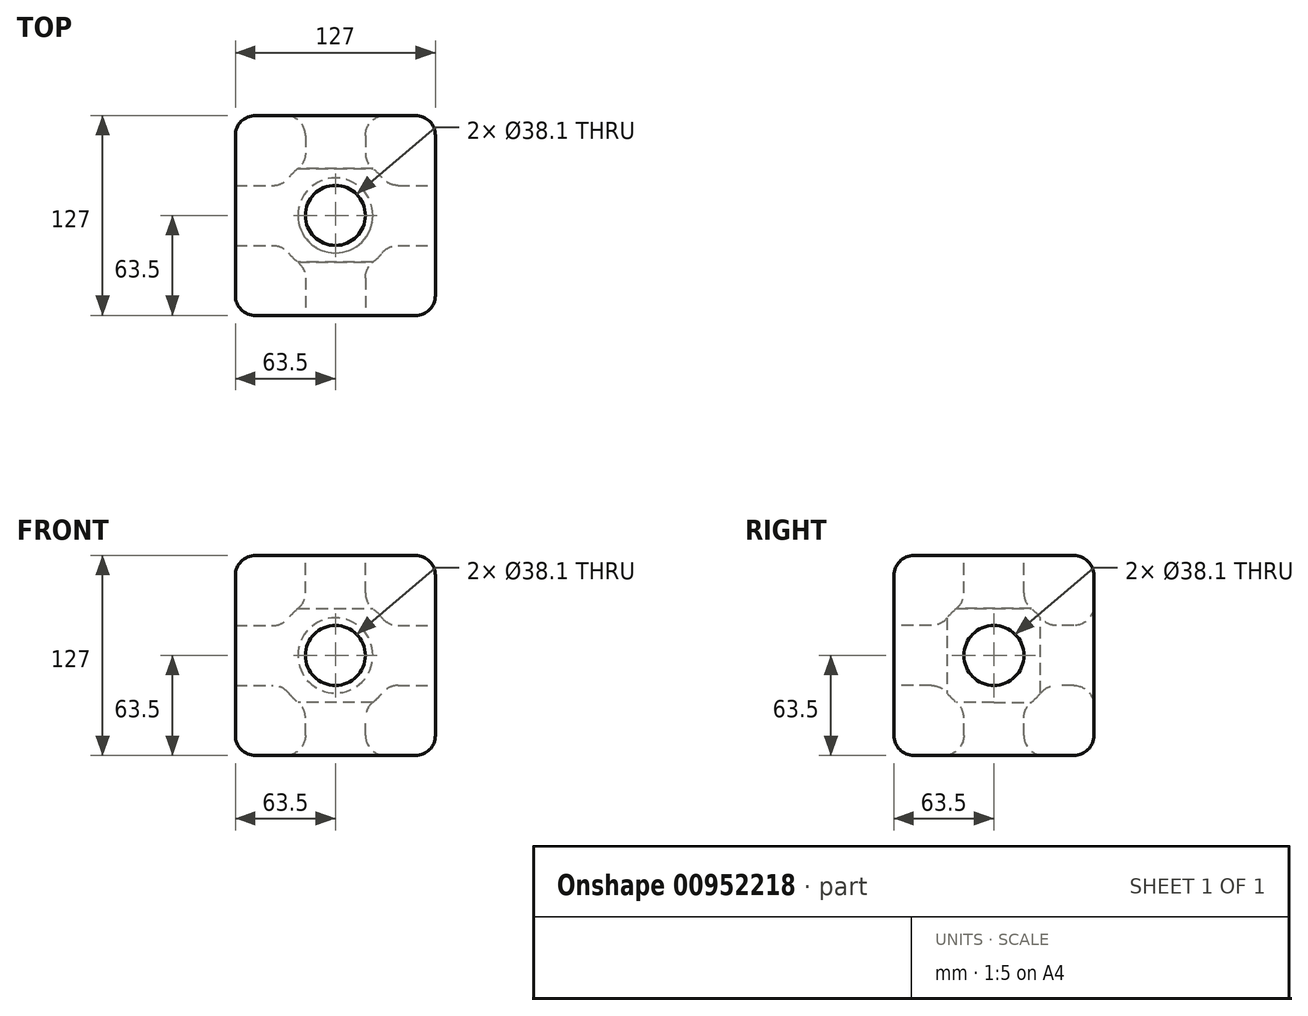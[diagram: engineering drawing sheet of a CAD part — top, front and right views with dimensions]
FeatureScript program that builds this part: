
annotation { "Feature Type Name" : "Feature", "Feature Type Description" : "" }
export const myFeature = defineFeature(function(context is Context, id is Id, definition is map)
    precondition{}
    {
        {
            var Q0;
            Q0=qCreatedBy(makeId("Top.planeOp"),FACE);
            var sketch = newSketch(context, id + "F0", { "sketchPlane" : qUnion([Q0])});
            skLineSegment(sketch, "E0.top", {"start": v(0, 63.5) * mm, "end": v(-63.5, 63.5) * mm});
            skLineSegment(sketch, "E0.right", {"start": v(-63.5, 0) * mm, "end": v(-63.5, 63.5) * mm});
            skLineSegment(sketch, "E1.MirrorCS", {"start": v(0, 63.5) * mm, "end": v(63.5, 63.5) * mm});
            skLineSegment(sketch, "E2.MirrorCS", {"start": v(63.5, 0) * mm, "end": v(63.5, 63.5) * mm});
            skLineSegment(sketch, "E3.MirrorCS", {"start": v(-63.5, 0) * mm, "end": v(-63.5, -63.5) * mm});
            skLineSegment(sketch, "E4.MirrorCS", {"start": v(0, -63.5) * mm, "end": v(-63.5, -63.5) * mm});
            skLineSegment(sketch, "E5.MirrorCS", {"start": v(0, -63.5) * mm, "end": v(63.5, -63.5) * mm});
            skLineSegment(sketch, "E6.MirrorCS", {"start": v(63.5, 0) * mm, "end": v(63.5, -63.5) * mm});
            skSolve(sketch);
        }
        {
            var Q0;
            Q0 = qSketchRegion(id + "F0", true);
            extrude(context, id + "F1", {"entities" : qUnion([Q0]), "endBound" : BoundingType.SYMMETRIC, "depth" : 127 * mm, "offsetDistance" : 25.4 * mm});
        }
        {
            var Q0;
            Q0=qCreatedBy(makeId("Top.planeOp"),FACE);
            var sketch = newSketch(context, id + "F2", { "sketchPlane" : qUnion([Q0])});
            skArc(sketch, "E7", {"start": v(38.1, 0) * mm, "mid": v(0, 38.1) * mm, "end": v(-38.1, 0) * mm});
            skLineSegment(sketch, "E8", {"start": v(-38.1, 0) * mm, "end": v(38.1, 0) * mm});
            skSolve(sketch);
        }
        {
            var Q0;
            Q0 = qSketchRegion(id + "F2", true);
            var Q1;
            Q1=sQuery(id+"F2.wireOp",EDGE,"E8");
            revolve(context, id + "F3", {"operationType" : NewBodyOperationType.REMOVE, "surfaceOperationType" : NewSurfaceOperationType.NEW, "entities" : qUnion([Q0]), "axis" : qUnion([Q1]), "revolveType" : RevolveType.FULL, "oppositeDirection" : true});
        }
        {
            var Q0;
            Q0=makeQuery(id+"F1.opExtrude","CAP_FACE",FACE,{"disambiguationData":[OSD([sQuery(id+"F0.wireOp",EDGE,"E0.top"),sQuery(id+"F0.wireOp",EDGE,"E0.right"),sQuery(id+"F0.wireOp",EDGE,"E1.MirrorCS"),sQuery(id+"F0.wireOp",EDGE,"E2.MirrorCS"),sQuery(id+"F0.wireOp",EDGE,"E3.MirrorCS"),sQuery(id+"F0.wireOp",EDGE,"E4.MirrorCS"),sQuery(id+"F0.wireOp",EDGE,"E5.MirrorCS"),sQuery(id+"F0.wireOp",EDGE,"E6.MirrorCS")])],"isStart":false});
            var sketch = newSketch(context, id + "F4", { "sketchPlane" : qUnion([Q0])});
            skCircle(sketch, "E9", {"center": v(0, 0) * mm, "radius": 19.05 * mm});
            skSolve(sketch);
        }
        {
            var Q0;
            Q0 = qSketchRegion(id + "F4", true);
            extrude(context, id + "F5", {"entities" : qUnion([Q0]), "operationType" : NewBodyOperationType.REMOVE, "oppositeDirection" : true, "depth" : 135.64 * mm, "offsetDistance" : 25.4 * mm});
        }
        {
            var Q0;
            Q0=makeQuery(id+"F1.opExtrude","SWEPT_FACE",FACE,{"disambiguationData":[OSD([sQuery(id+"F0.wireOp",EDGE,"E4.MirrorCS"),sQuery(id+"F0.wireOp",EDGE,"E5.MirrorCS")])]});
            var sketch = newSketch(context, id + "F6", { "sketchPlane" : qUnion([Q0])});
            skCircle(sketch, "E10", {"center": v(0, 0) * mm, "radius": 19.05 * mm});
            skSolve(sketch);
        }
        {
            var Q0;
            Q0 = qSketchRegion(id + "F6", true);
            extrude(context, id + "F7", {"entities" : qUnion([Q0]), "operationType" : NewBodyOperationType.REMOVE, "oppositeDirection" : true, "depth" : 145.8 * mm, "offsetDistance" : 25.4 * mm});
        }
        {
            var Q0;
            Q0=makeQuery(id+"F1.opExtrude","CAP_EDGE",EDGE,{"disambiguationData":[OSD([sQuery(id+"F0.wireOp",EDGE,"E0.right"),sQuery(id+"F0.wireOp",EDGE,"E3.MirrorCS")])],"isStart":true});
            var Q1;
            Q1=makeQuery(id+"F1.opExtrude","CAP_EDGE",EDGE,{"disambiguationData":[OSD([sQuery(id+"F0.wireOp",EDGE,"E0.top"),sQuery(id+"F0.wireOp",EDGE,"E1.MirrorCS")])],"isStart":true});
            var Q2;
            Q2=makeQuery(id+"F1.opExtrude","CAP_EDGE",EDGE,{"disambiguationData":[OSD([sQuery(id+"F0.wireOp",EDGE,"E2.MirrorCS"),sQuery(id+"F0.wireOp",EDGE,"E6.MirrorCS")])],"isStart":true});
            var Q3;
            Q3=makeQuery(id+"F1.opExtrude","SWEPT_EDGE",EDGE,{"disambiguationData":[OSD([sQuery(id+"F0.wireOp",EDGE,"E1.MirrorCS"),sQuery(id+"F0.wireOp",EDGE,"E2.MirrorCS")])]});
            var Q4;
            Q4=makeQuery(id+"F1.opExtrude","CAP_EDGE",EDGE,{"disambiguationData":[OSD([sQuery(id+"F0.wireOp",EDGE,"E2.MirrorCS"),sQuery(id+"F0.wireOp",EDGE,"E6.MirrorCS")])],"isStart":false});
            var Q5;
            Q5=makeQuery(id+"F1.opExtrude","CAP_EDGE",EDGE,{"disambiguationData":[OSD([sQuery(id+"F0.wireOp",EDGE,"E0.top"),sQuery(id+"F0.wireOp",EDGE,"E1.MirrorCS")])],"isStart":false});
            var Q6;
            Q6=makeQuery(id+"F1.opExtrude","SWEPT_EDGE",EDGE,{"disambiguationData":[OSD([sQuery(id+"F0.wireOp",EDGE,"E5.MirrorCS"),sQuery(id+"F0.wireOp",EDGE,"E6.MirrorCS")])]});
            var Q7;
            Q7=makeQuery(id+"F1.opExtrude","CAP_EDGE",EDGE,{"disambiguationData":[OSD([sQuery(id+"F0.wireOp",EDGE,"E4.MirrorCS"),sQuery(id+"F0.wireOp",EDGE,"E5.MirrorCS")])],"isStart":false});
            var Q8;
            Q8=makeQuery(id+"F1.opExtrude","CAP_EDGE",EDGE,{"disambiguationData":[OSD([sQuery(id+"F0.wireOp",EDGE,"E4.MirrorCS"),sQuery(id+"F0.wireOp",EDGE,"E5.MirrorCS")])],"isStart":true});
            var Q9;
            Q9=makeQuery(id+"F1.opExtrude","SWEPT_EDGE",EDGE,{"disambiguationData":[OSD([sQuery(id+"F0.wireOp",EDGE,"E3.MirrorCS"),sQuery(id+"F0.wireOp",EDGE,"E4.MirrorCS")])]});
            var Q10;
            Q10=makeQuery(id+"F1.opExtrude","SWEPT_EDGE",EDGE,{"disambiguationData":[OSD([sQuery(id+"F0.wireOp",EDGE,"E0.top"),sQuery(id+"F0.wireOp",EDGE,"E0.right")])]});
            var Q11;
            Q11=makeQuery(id+"F1.opExtrude","CAP_EDGE",EDGE,{"disambiguationData":[OSD([sQuery(id+"F0.wireOp",EDGE,"E0.right"),sQuery(id+"F0.wireOp",EDGE,"E3.MirrorCS")])],"isStart":false});
            var Q12;
            Q12=makeQuery(id+"F5.boolean.opBoolean","COPY",EDGE,{"derivedFrom":makeQuery(id+"F5.opExtrude","CAP_EDGE",EDGE,{"disambiguationData":[OSD([sQuery(id+"F4.wireOp",EDGE,"E9")])],"isStart":true})});
            var Q13;
            Q13=makeQuery(id+"F7.boolean.opBoolean","INTERSECT",EDGE,{"derivedFrom":[makeQuery(id+"F1.opExtrude","SWEPT_FACE",FACE,{"disambiguationData":[OSD([sQuery(id+"F0.wireOp",EDGE,"E0.top"),sQuery(id+"F0.wireOp",EDGE,"E1.MirrorCS")])]}),makeQuery(id+"F7.opExtrude","SWEPT_FACE",FACE,{"disambiguationData":[OSD([sQuery(id+"F6.wireOp",EDGE,"E10")])]})]});
            var Q14;
            Q14=makeQuery(id+"F5.boolean.opBoolean","INTERSECT",EDGE,{"derivedFrom":[makeQuery(id+"F1.opExtrude","CAP_FACE",FACE,{"disambiguationData":[OSD([sQuery(id+"F0.wireOp",EDGE,"E0.top"),sQuery(id+"F0.wireOp",EDGE,"E0.right"),sQuery(id+"F0.wireOp",EDGE,"E1.MirrorCS"),sQuery(id+"F0.wireOp",EDGE,"E2.MirrorCS"),sQuery(id+"F0.wireOp",EDGE,"E3.MirrorCS"),sQuery(id+"F0.wireOp",EDGE,"E4.MirrorCS"),sQuery(id+"F0.wireOp",EDGE,"E5.MirrorCS"),sQuery(id+"F0.wireOp",EDGE,"E6.MirrorCS")])],"isStart":true}),makeQuery(id+"F5.opExtrude","SWEPT_FACE",FACE,{"disambiguationData":[OSD([sQuery(id+"F4.wireOp",EDGE,"E9")])]})]});
            var Q15;
            Q15=makeQuery(id+"F7.boolean.opBoolean","COPY",EDGE,{"derivedFrom":makeQuery(id+"F7.opExtrude","CAP_EDGE",EDGE,{"disambiguationData":[OSD([sQuery(id+"F6.wireOp",EDGE,"E10")])],"isStart":true})});
            var Q16;
            Q16=makeQuery(id+"F7.boolean.opBoolean","INTERSECT",EDGE,{"disambiguationData":[OD(0.0)],"derivedFrom":[makeQuery(id+"F3.boolean.opBoolean","COPY",FACE,{"derivedFrom":makeQuery(id+"F3.opRevolve","SWEPT_FACE",FACE,{"disambiguationData":[OSD([sQuery(id+"F2.wireOp",EDGE,"E7")])]})}),makeQuery(id+"F7.opExtrude","SWEPT_FACE",FACE,{"disambiguationData":[OSD([sQuery(id+"F6.wireOp",EDGE,"E10")])]})]});
            var Q17;
            Q17=makeQuery(id+"F5.boolean.opBoolean","INTERSECT",EDGE,{"disambiguationData":[OD(0.0)],"derivedFrom":[makeQuery(id+"F3.boolean.opBoolean","COPY",FACE,{"derivedFrom":makeQuery(id+"F3.opRevolve","SWEPT_FACE",FACE,{"disambiguationData":[OSD([sQuery(id+"F2.wireOp",EDGE,"E7")])]})}),makeQuery(id+"F5.opExtrude","SWEPT_FACE",FACE,{"disambiguationData":[OSD([sQuery(id+"F4.wireOp",EDGE,"E9")])]})]});
            var Q18;
            Q18=makeQuery(id+"F7.boolean.opBoolean","INTERSECT",EDGE,{"disambiguationData":[OD(1.0)],"derivedFrom":[makeQuery(id+"F3.boolean.opBoolean","COPY",FACE,{"derivedFrom":makeQuery(id+"F3.opRevolve","SWEPT_FACE",FACE,{"disambiguationData":[OSD([sQuery(id+"F2.wireOp",EDGE,"E7")])]})}),makeQuery(id+"F7.opExtrude","SWEPT_FACE",FACE,{"disambiguationData":[OSD([sQuery(id+"F6.wireOp",EDGE,"E10")])]})]});
            var Q19;
            Q19=makeQuery(id+"F5.boolean.opBoolean","INTERSECT",EDGE,{"disambiguationData":[OD(1.0)],"derivedFrom":[makeQuery(id+"F3.boolean.opBoolean","COPY",FACE,{"derivedFrom":makeQuery(id+"F3.opRevolve","SWEPT_FACE",FACE,{"disambiguationData":[OSD([sQuery(id+"F2.wireOp",EDGE,"E7")])]})}),makeQuery(id+"F5.opExtrude","SWEPT_FACE",FACE,{"disambiguationData":[OSD([sQuery(id+"F4.wireOp",EDGE,"E9")])]})]});
            fillet(context, id + "F8", {"entities" : qUnion([Q0, Q1, Q2, Q3, Q4, Q5, Q6, Q7, Q8, Q9, Q10, Q11, Q12, Q13, Q14, Q15, Q16, Q17, Q18, Q19]), "radius" : 12.7 * mm, "tangentPropagation" : true, "allowEdgeOverflow" : false});
        }
        {
            var Q0;
            Q0=makeQuery(id+"F1.opExtrude","SWEPT_FACE",FACE,{"disambiguationData":[OSD([sQuery(id+"F0.wireOp",EDGE,"E2.MirrorCS"),sQuery(id+"F0.wireOp",EDGE,"E6.MirrorCS")])]});
            var sketch = newSketch(context, id + "F9", { "sketchPlane" : qUnion([Q0])});
            skCircle(sketch, "E11", {"center": v(0, 0) * mm, "radius": 19.05 * mm});
            skSolve(sketch);
        }
        {
            var Q0;
            Q0 = qSketchRegion(id + "F9", true);
            extrude(context, id + "F10", {"entities" : qUnion([Q0]), "operationType" : NewBodyOperationType.REMOVE, "oppositeDirection" : true, "depth" : 127 * mm, "offsetDistance" : 25.4 * mm});
        }
        {
            var Q0;
            Q0=makeQuery(id+"F10.boolean.opBoolean","COPY",EDGE,{"derivedFrom":makeQuery(id+"F10.opExtrude","CAP_EDGE",EDGE,{"disambiguationData":[OSD([sQuery(id+"F9.wireOp",EDGE,"E11")])],"isStart":true})});
            var Q1;
            Q1=makeQuery(id+"F10.boolean.opBoolean","INTERSECT",EDGE,{"disambiguationData":[OD(0.0)],"derivedFrom":[makeQuery(id+"F3.boolean.opBoolean","COPY",FACE,{"derivedFrom":makeQuery(id+"F3.opRevolve","SWEPT_FACE",FACE,{"disambiguationData":[OSD([sQuery(id+"F2.wireOp",EDGE,"E7")])]})}),makeQuery(id+"F10.opExtrude","SWEPT_FACE",FACE,{"disambiguationData":[OSD([sQuery(id+"F9.wireOp",EDGE,"E11")])]})]});
            var Q2;
            Q2=makeQuery(id+"F10.boolean.opBoolean","COPY",EDGE,{"derivedFrom":makeQuery(id+"F10.opExtrude","CAP_EDGE",EDGE,{"disambiguationData":[OSD([sQuery(id+"F9.wireOp",EDGE,"E11")])],"isStart":false})});
            var Q3;
            Q3=makeQuery(id+"F10.boolean.opBoolean","INTERSECT",EDGE,{"disambiguationData":[OD(1.0)],"derivedFrom":[makeQuery(id+"F3.boolean.opBoolean","COPY",FACE,{"derivedFrom":makeQuery(id+"F3.opRevolve","SWEPT_FACE",FACE,{"disambiguationData":[OSD([sQuery(id+"F2.wireOp",EDGE,"E7")])]})}),makeQuery(id+"F10.opExtrude","SWEPT_FACE",FACE,{"disambiguationData":[OSD([sQuery(id+"F9.wireOp",EDGE,"E11")])]})]});
            fillet(context, id + "F11", {"entities" : qUnion([Q0, Q1, Q2, Q3]), "radius" : 12.7 * mm, "tangentPropagation" : true, "allowEdgeOverflow" : false});
        }
    });
